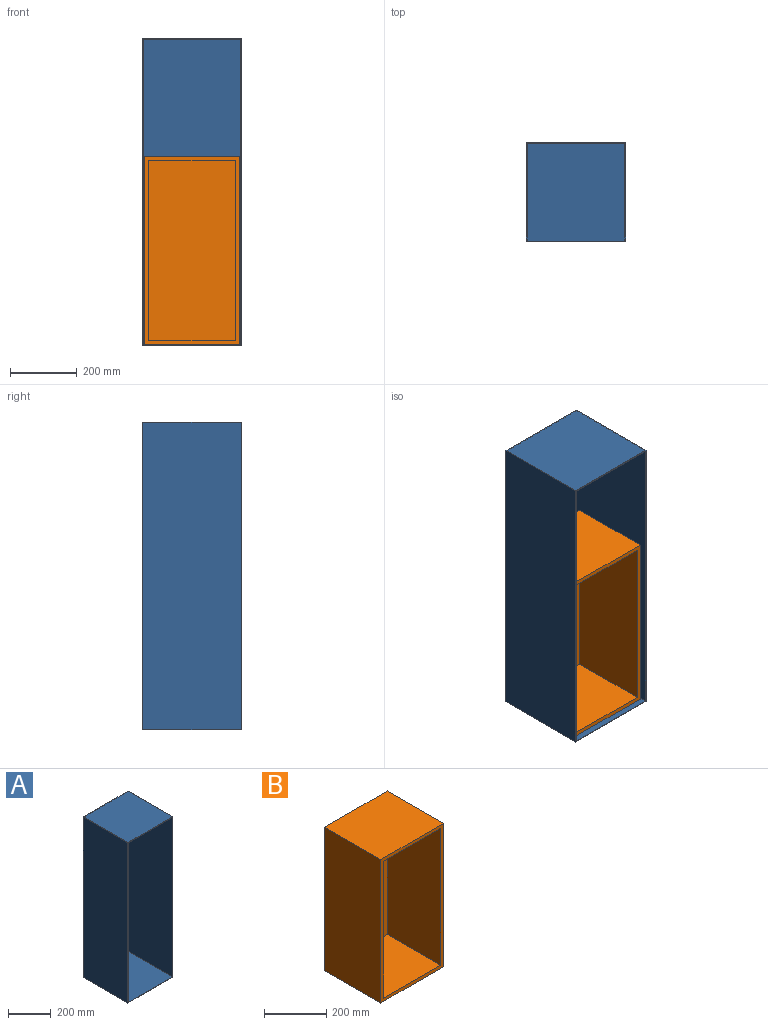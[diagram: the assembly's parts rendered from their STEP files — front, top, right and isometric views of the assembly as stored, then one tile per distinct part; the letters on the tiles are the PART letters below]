
ASSEMBLY  parts=2 mates=1
PART A: 11 faces, bbox 297.2x294.6x919.5 mm
  f0: plane 919.48x297.18mm, normal (0,-1,0), area 6154.8mm2, adj f1,f2,f3,f4,f6,f7,f8,f9
  f1: plane 919.48x294.64mm, normal (-1,0,0), area 270915.6mm2, adj f0,f2,f4,f5
  f2: plane 297.18x294.64mm, normal (0,0,-1), area 87561.1mm2, adj f0,f1,f3,f5
  f3: plane 919.48x294.64mm, normal (1,0,0), area 270915.6mm2, adj f0,f2,f4,f5
  f4: plane 297.18x294.64mm, normal (0,0,1), area 87561.1mm2, adj f0,f1,f3,f5
  f5: plane 919.48x297.18mm, normal (0,1,0), area 273251.1mm2, adj f1,f2,f3,f4
  f6: plane 914.4x292.1mm, normal (1,0,0), area 267096.2mm2, adj f0,f7,f9,f10
  f7: plane 292.1x292.1mm, normal (0,0,1), area 85322.4mm2, adj f0,f6,f8,f10
  f8: plane 914.4x292.1mm, normal (-1,0,0), area 267096.2mm2, adj f0,f7,f9,f10
  f9: plane 292.1x292.1mm, normal (0,0,-1), area 85322.4mm2, adj f0,f6,f8,f10
  f10: plane 914.4x292.1mm, normal (0,-1,0), area 267096.2mm2, adj f6,f7,f8,f9
PART B: 11 faces, bbox 284.5x255.3x563.9 mm
  f0: plane 563.88x284.48mm, normal (0,-1,0), area 20903.2mm2, adj f1,f2,f3,f4,f6,f7,f8,f9
  f1: plane 563.88x255.27mm, normal (-1,0,0), area 143941.6mm2, adj f0,f2,f4,f5
  f2: plane 284.48x255.27mm, normal (0,0,-1), area 72619.2mm2, adj f0,f1,f3,f5
  f3: plane 563.88x255.27mm, normal (1,0,0), area 143941.6mm2, adj f0,f2,f4,f5
  f4: plane 284.48x255.27mm, normal (0,0,1), area 72619.2mm2, adj f0,f1,f3,f5
  f5: plane 563.88x284.48mm, normal (0,1,0), area 160412.6mm2, adj f1,f2,f3,f4
  f6: plane 538.48x242.57mm, normal (1,0,0), area 130619.1mm2, adj f0,f7,f9,f10
  f7: plane 259.08x242.57mm, normal (0,0,1), area 62845mm2, adj f0,f6,f8,f10
  f8: plane 538.48x242.57mm, normal (-1,0,0), area 130619.1mm2, adj f0,f7,f9,f10
  f9: plane 259.08x242.57mm, normal (0,0,-1), area 62845mm2, adj f0,f6,f8,f10
  f10: plane 538.48x259.08mm, normal (0,-1,0), area 139509.4mm2, adj f6,f7,f8,f9
PLACE A t=(-250.98,-1140.43,88.82)mm
PLACE B t=(-431.77,-1158.85,-92.83)mm
MATE fastened B.f2 <-> A.f7  axis (0,0,-1) through (-500.23,-1286.48,-376.31)mm
